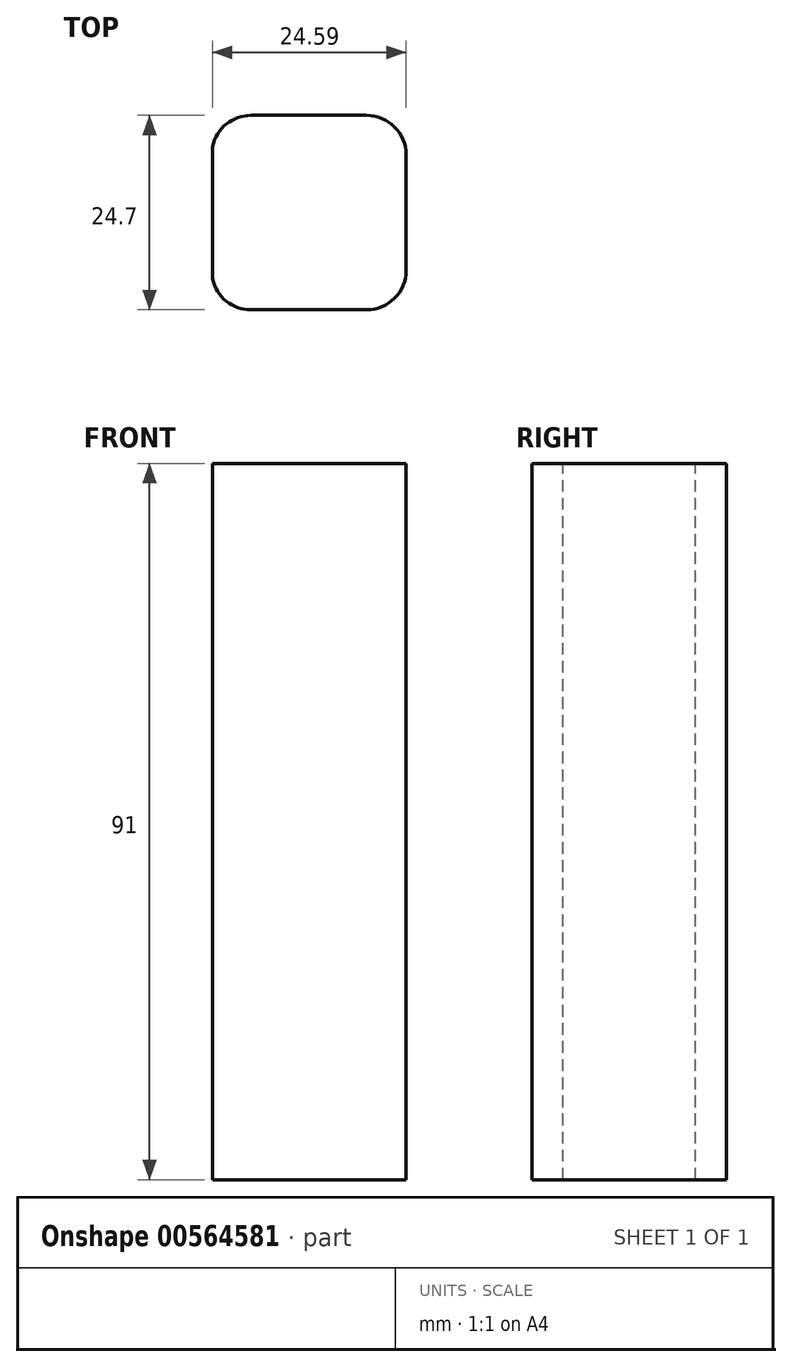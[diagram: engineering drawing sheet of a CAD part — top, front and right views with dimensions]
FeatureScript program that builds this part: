
annotation { "Feature Type Name" : "Feature", "Feature Type Description" : "" }
export const myFeature = defineFeature(function(context is Context, id is Id, definition is map)
    precondition{}
    {
        {
            var Q0;
            Q0=qCreatedBy(makeId("Top.planeOp"),FACE);
            var sketch = newSketch(context, id + "F0", { "sketchPlane" : qUnion([Q0])});
            skLineSegment(sketch, "E0.bottom", {"start": v(-40, 30) * mm, "end": v(40, 30) * mm});
            skLineSegment(sketch, "E0.top", {"start": v(-40, -30) * mm, "end": v(40, -30) * mm});
            skLineSegment(sketch, "E0.left", {"start": v(-40, 30) * mm, "end": v(-40, -30) * mm});
            skLineSegment(sketch, "E0.right", {"start": v(40, 30) * mm, "end": v(40, -30) * mm});
            skPoint(sketch, "E0.middle", {"position": v(0, 0) * mm});
            skSolve(sketch);
        }
        {
            var Q0;
            Q0=makeQuery(id+"F0.imprint","IMPRINT",FACE,{"disambiguationData":[TD([[makeQuery(id+"F0.imprint","IMPRINT",EDGE,{"derivedFrom":sQuery(id+"F0.wireOp",EDGE,"E0.bottom")}),-1.0]])]});
            extrude(context, id + "F1", {"entities" : qUnion([Q0]), "depth" : 130 * mm});
        }
        {
            var Q0;
            Q0=makeQuery(id+"F1.opExtrude","CAP_FACE",FACE,{"disambiguationData":[OSD([sQuery(id+"F0.wireOp",EDGE,"E0.bottom"),sQuery(id+"F0.wireOp",EDGE,"E0.top"),sQuery(id+"F0.wireOp",EDGE,"E0.left"),sQuery(id+"F0.wireOp",EDGE,"E0.right")])],"isStart":false});
            shell(context, id + "F2", {"entities" : qUnion([Q0]), "thickness" : 1.5 * mm});
        }
        {
            var Q0;
            Q0=makeQuery(id+"F2.opShell","OFFSET_FACE",FACE,{"disambiguationData":[OSD([sQuery(id+"F0.wireOp",EDGE,"E0.bottom"),sQuery(id+"F0.wireOp",EDGE,"E0.top"),sQuery(id+"F0.wireOp",EDGE,"E0.left"),sQuery(id+"F0.wireOp",EDGE,"E0.right")])]});
            var sketch = newSketch(context, id + "F3", { "sketchPlane" : qUnion([Q0])});
            skLineSegment(sketch, "E1.bottom", {"start": v(11, -28.5) * mm, "end": v(12.5, -28.5) * mm});
            skLineSegment(sketch, "E1.top", {"start": v(11, -1.5) * mm, "end": v(12.5, -1.5) * mm});
            skLineSegment(sketch, "E1.left", {"start": v(11, -28.5) * mm, "end": v(11, -1.5) * mm});
            skLineSegment(sketch, "E1.right", {"start": v(12.5, -28.5) * mm, "end": v(12.5, -1.5) * mm});
            skSolve(sketch);
        }
        {
            var Q0;
            Q0=qSketchRegion(id+"F3",true);
            extrude(context, id + "F4", {"entities" : qUnion([Q0]), "operationType" : NewBodyOperationType.ADD, "depth" : 91 * mm});
        }
        {
            var Q0;
            {var subQ0=sQuery(id+"F0.wireOp",EDGE,"E0.bottom");Q0=makeQuery(id+"F2.opShell","OFFSET_EDGE",EDGE,{"disambiguationData":[OSD([subQ0]),TDD([makeQuery(id+"F1.opExtrude","CAP_EDGE",EDGE,{"disambiguationData":[OSD([subQ0])],"isStart":true})])]});}
            var Q1;
            {var subQ0=sQuery(id+"F0.wireOp",EDGE,"E0.left");Q1=makeQuery(id+"F2.opShell","OFFSET_EDGE",EDGE,{"disambiguationData":[OSD([subQ0]),TDD([makeQuery(id+"F1.opExtrude","CAP_EDGE",EDGE,{"disambiguationData":[OSD([subQ0])],"isStart":true})])]});}
            var Q2;
            {var subQ0=sQuery(id+"F0.wireOp",EDGE,"E0.left");var subQ1=sQuery(id+"F0.wireOp",EDGE,"E0.top");Q2=makeQuery(id+"F4.boolean.opBoolean","SPLIT",EDGE,{"disambiguationData":[TD([makeQuery(id+"F2.opShell","OFFSET_FACE",FACE,{"disambiguationData":[OSD([subQ0])]})])],"derivedFrom":makeQuery(id+"F2.opShell","OFFSET_EDGE",EDGE,{"disambiguationData":[OSD([subQ1]),TDD([makeQuery(id+"F1.opExtrude","CAP_EDGE",EDGE,{"disambiguationData":[OSD([subQ1])],"isStart":true})])]})});}
            var Q3;
            Q3=makeQuery(id+"F4.opExtrude","CAP_EDGE",EDGE,{"disambiguationData":[OSD([sQuery(id+"F3.wireOp",EDGE,"E1.left")])],"isStart":true});
            fillet(context, id + "F5", {"entities" : qUnion([Q0, Q1, Q2, Q3]), "radius" : 1 * mm, "tangentPropagation" : true, "allowEdgeOverflow" : false});
        }
        {
            var Q0;
            Q0=makeQuery(id+"F4.opExtrude","CAP_FACE",FACE,{"disambiguationData":[OSD([sQuery(id+"F3.wireOp",EDGE,"E1.bottom"),sQuery(id+"F3.wireOp",EDGE,"E1.top"),sQuery(id+"F3.wireOp",EDGE,"E1.left"),sQuery(id+"F3.wireOp",EDGE,"E1.right")])],"isStart":false});
            var sketch = newSketch(context, id + "F6", { "sketchPlane" : qUnion([Q0])});
            skLineSegment(sketch, "E2.bottom", {"start": v(11, -1.5) * mm, "end": v(38.47, -1.5) * mm});
            skLineSegment(sketch, "E2.top", {"start": v(11, -28.53) * mm, "end": v(38.47, -28.53) * mm});
            skLineSegment(sketch, "E2.left", {"start": v(11, -1.5) * mm, "end": v(11, -28.53) * mm});
            skLineSegment(sketch, "E2.right", {"start": v(38.47, -1.5) * mm, "end": v(38.47, -28.53) * mm});
            skLineSegment(sketch, "E3.bottom", {"start": v(33.24, -7) * mm, "end": v(16.24, -7) * mm});
            skLineSegment(sketch, "E3.top", {"start": v(33.24, -23) * mm, "end": v(16.24, -23) * mm});
            skLineSegment(sketch, "E3.left", {"start": v(33.24, -7) * mm, "end": v(33.24, -23) * mm});
            skLineSegment(sketch, "E3.right", {"start": v(16.24, -7) * mm, "end": v(16.24, -23) * mm});
            skPoint(sketch, "E3.middle", {"position": v(24.74, -15) * mm});
            skPoint(sketch, "E3.middle.positionSnap0", {"position": v(12.5, -15) * mm});
            skPoint(sketch, "E3.middle.positionSnap1", {"position": v(24.74, -1.5) * mm});
            skPoint(sketch, "E3.centerSnap0", {"position": v(12.5, -15) * mm});
            skPoint(sketch, "E3.centerSnap1", {"position": v(24.74, -1.5) * mm});
            skSolve(sketch);
        }
        {
            var Q0;
            {var subQ0=sQuery(id+"F6.wireOp",EDGE,"E2.top");Q0=makeQuery(id+"F6.imprint","IMPRINT",FACE,{"disambiguationData":[TD([[makeQuery(id+"F6.imprint","IMPRINT",EDGE,{"derivedFrom":subQ0}),1.0]])]});}
            var Q1;
            {var subQ3=makeQuery(id+"F4.opExtrude","CAP_EDGE",EDGE,{"disambiguationData":[OSD([sQuery(id+"F3.wireOp",EDGE,"E1.right")])],"isStart":false});Q1=makeQuery(id+"F6.imprint","IMPRINT",FACE,{"disambiguationData":[TD([[makeQuery(id+"F6.imprint","IMPRINT",EDGE,{"derivedFrom":subQ3}),1.0]])]});}
            extrude(context, id + "F7", {"entities" : qUnion([Q0, Q1]), "operationType" : NewBodyOperationType.ADD, "depth" : 2 * mm});
        }
        {
            var Q0;
            Q0=makeQuery(id+"F7.boolean.opBoolean","INTERSECT",EDGE,{"derivedFrom":[makeQuery(id+"F2.opShell","OFFSET_FACE",FACE,{"disambiguationData":[OSD([sQuery(id+"F0.wireOp",EDGE,"E0.top")])]}),makeQuery(id+"F7.opExtrude","SWEPT_FACE",FACE,{"disambiguationData":[OSD([sQuery(id+"F6.wireOp",EDGE,"E2.left")])]})]});
            var Q1;
            Q1=makeQuery(id+"F7.boolean.opBoolean","INTERSECT",EDGE,{"derivedFrom":[makeQuery(id+"F2.opShell","OFFSET_FACE",FACE,{"disambiguationData":[OSD([sQuery(id+"F0.wireOp",EDGE,"E0.top")])]}),makeQuery(id+"F7.opExtrude","CAP_FACE",FACE,{"disambiguationData":[OSD([sQuery(id+"F6.wireOp",EDGE,"E2.bottom"),sQuery(id+"F6.wireOp",EDGE,"E2.top"),sQuery(id+"F6.wireOp",EDGE,"E2.left"),sQuery(id+"F6.wireOp",EDGE,"E2.right"),sQuery(id+"F6.wireOp",EDGE,"E3.bottom"),sQuery(id+"F6.wireOp",EDGE,"E3.top"),sQuery(id+"F6.wireOp",EDGE,"E3.left"),sQuery(id+"F6.wireOp",EDGE,"E3.right")])],"isStart":false})]});
            fillet(context, id + "F8", {"entities" : qUnion([Q0, Q1]), "radius" : 1 * mm, "tangentPropagation" : true, "allowEdgeOverflow" : false});
        }
        {
            var Q0;
            {var subQ0=sQuery(id+"F0.wireOp",EDGE,"E0.left");var subQ1=sQuery(id+"F0.wireOp",EDGE,"E0.top");Q0=makeQuery(id+"FWzvhFEn40ZoO8K_2.boolean.opBoolean","SPLIT",EDGE,{"disambiguationData":[TD([makeQuery(id+"F5.opFillet","BLEND_FACE",FACE,{"disambiguationData":[OSD([subQ0])]})])],"derivedFrom":makeQuery(id+"F2.opShell","OFFSET_EDGE",EDGE,{"disambiguationData":[OSD([subQ1,subQ0])]})});}
            var Q1;
            {var subQ0=sQuery(id+"F0.wireOp",EDGE,"E0.left");var subQ1=sQuery(id+"F0.wireOp",EDGE,"E0.bottom");Q1=makeQuery(id+"FWzvhFEn40ZoO8K_2.boolean.opBoolean","SPLIT",EDGE,{"disambiguationData":[TD([makeQuery(id+"F5.opFillet","BLEND_FACE",FACE,{"disambiguationData":[OSD([subQ1])]})])],"derivedFrom":makeQuery(id+"F2.opShell","OFFSET_EDGE",EDGE,{"disambiguationData":[OSD([subQ1,subQ0])]})});}
            var Q2;
            {var subQ0=sQuery(id+"F0.wireOp",EDGE,"E0.bottom");var subQ1=sQuery(id+"F0.wireOp",EDGE,"E0.right");Q2=makeQuery(id+"FWzvhFEn40ZoO8K_2.boolean.opBoolean","SPLIT",EDGE,{"disambiguationData":[TD([makeQuery(id+"F5.opFillet","BLEND_FACE",FACE,{"disambiguationData":[OSD([subQ0])]})])],"derivedFrom":makeQuery(id+"F2.opShell","OFFSET_EDGE",EDGE,{"disambiguationData":[OSD([subQ0,subQ1])]})});}
            fillet(context, id + "F9", {"entities" : qUnion([Q0, Q1, Q2]), "radius" : 1 * mm, "tangentPropagation" : true, "allowEdgeOverflow" : false});
        }
        {
            var Q0;
            Q0=makeQuery(id+"F1.opExtrude","SWEPT_FACE",FACE,{"disambiguationData":[OSD([sQuery(id+"F0.wireOp",EDGE,"E0.bottom")])]});
            var sketch = newSketch(context, id + "F10", { "sketchPlane" : qUnion([Q0])});
            skLineSegment(sketch, "E4.0", {"start": v(-41.4, 2.4) * mm, "end": v(-65.42, 34.39) * mm});
            skLineSegment(sketch, "E5", {"start": v(-41.4, 2.4) * mm, "end": v(-42.6, 1.5) * mm});
            skLineSegment(sketch, "E6", {"start": v(-65.42, 34.39) * mm, "end": v(-66.62, 33.49) * mm});
            skLineSegment(sketch, "E7", {"start": v(-42.6, 1.5) * mm, "end": v(-66.62, 33.49) * mm});
            skLineSegment(sketch, "E8.bottom", {"start": v(-40, 0) * mm, "end": v(-45, 0) * mm});
            skLineSegment(sketch, "E8.top", {"start": v(-40, 4) * mm, "end": v(-45, 4) * mm});
            skLineSegment(sketch, "E8.left", {"start": v(-40, 0) * mm, "end": v(-40, 4) * mm});
            skLineSegment(sketch, "E8.right", {"start": v(-45, 0) * mm, "end": v(-45, 4) * mm});
            skLineSegment(sketch, "E9.bottom", {"start": v(-40, 32.63) * mm, "end": v(-68, 32.63) * mm});
            skLineSegment(sketch, "E9.top", {"start": v(-40, 35.63) * mm, "end": v(-68, 35.63) * mm});
            skLineSegment(sketch, "E9.left", {"start": v(-40, 32.63) * mm, "end": v(-40, 35.63) * mm});
            skLineSegment(sketch, "E9.right", {"start": v(-68, 32.63) * mm, "end": v(-68, 35.63) * mm});
            skSolve(sketch);
        }
        {
            var Q0;
            {var subQ1=sQuery(id+"F10.wireOp",EDGE,"E5");Q0=makeQuery(id+"F10.imprint","IMPRINT",FACE,{"disambiguationData":[TD([[makeQuery(id+"F10.imprint","IMPRINT",EDGE,{"derivedFrom":subQ1}),1.0]])]});}
            extrude(context, id + "F11", {"entities" : qUnion([Q0]), "operationType" : NewBodyOperationType.ADD, "oppositeDirection" : true, "depth" : 60 * mm});
        }
        {
            var Q0;
            {var subQ1=sQuery(id+"F10.wireOp",EDGE,"E6");Q0=makeQuery(id+"F10.imprint","IMPRINT",FACE,{"disambiguationData":[TD([[makeQuery(id+"F10.imprint","IMPRINT",EDGE,{"derivedFrom":subQ1}),-1.0]])]});}
            extrude(context, id + "F12", {"entities" : qUnion([Q0]), "operationType" : NewBodyOperationType.ADD, "oppositeDirection" : true, "depth" : 60 * mm});
        }
        {
            var Q0;
            {var subQ0=sQuery(id+"F10.wireOp",EDGE,"E5");Q0=makeQuery(id+"F10.imprint","IMPRINT",FACE,{"disambiguationData":[TD([[makeQuery(id+"F10.imprint","IMPRINT",EDGE,{"derivedFrom":subQ0}),-1.0]])]});}
            var Q1;
            {var subQ0=sQuery(id+"F10.wireOp",EDGE,"E8.top");var subQ1=sQuery(id+"F10.wireOp",EDGE,"E4.0");var subQ2=makeQuery(id+"F10.imprint","INTERSECT",VERTEX,{"derivedFrom":[subQ1,subQ0]});Q1=makeQuery(id+"F10.imprint","IMPRINT",FACE,{"disambiguationData":[TD([[makeQuery(id+"F10.imprint","IMPRINT",EDGE,{"disambiguationData":[TD([[subQ2,-1.0]])],"derivedFrom":subQ1}),1.0]])]});}
            var Q2;
            {var subQ0=sQuery(id+"F10.wireOp",EDGE,"E6");Q2=makeQuery(id+"F10.imprint","IMPRINT",FACE,{"disambiguationData":[TD([[makeQuery(id+"F10.imprint","IMPRINT",EDGE,{"derivedFrom":subQ0}),1.0]])]});}
            var Q3;
            Q3=sQuery(id+"F10.wireOp",EDGE,"E7");
            var Q4;
            Q4=sQuery(id+"F10.wireOp",EDGE,"E4.0");
            var Q5;
            Q5=sQuery(id+"F10.wireOp",EDGE,"E6");
            var Q6;
            Q6=sQuery(id+"F10.wireOp",EDGE,"E5");
            extrude(context, id + "F13", {"entities" : qUnion([Q0, Q1, Q2]), "surfaceEntities" : qUnion([Q3, Q4, Q5, Q6]), "oppositeDirection" : true, "depth" : 50 * mm});
        }
        {
            var Q0;
            Q0=makeQuery(id+"F12.opExtrude","SWEPT_EDGE",EDGE,{"disambiguationData":[OSD([sQuery(id+"F0.wireOp",EDGE,"E0.bottom"),sQuery(id+"F0.wireOp",EDGE,"E0.right"),sQuery(id+"F10.wireOp",EDGE,"E9.top"),sQuery(id+"F10.wireOp",EDGE,"E9.left")])]});
            var Q1;
            Q1=makeQuery(id+"F11.opExtrude","SWEPT_EDGE",EDGE,{"disambiguationData":[OSD([sQuery(id+"F0.wireOp",EDGE,"E0.bottom"),sQuery(id+"F0.wireOp",EDGE,"E0.right"),sQuery(id+"F10.wireOp",EDGE,"E8.top"),sQuery(id+"F10.wireOp",EDGE,"E8.left")])]});
            var Q2;
            Q2=makeQuery(id+"F12.opExtrude","SWEPT_EDGE",EDGE,{"disambiguationData":[OSD([sQuery(id+"F0.wireOp",EDGE,"E0.bottom"),sQuery(id+"F0.wireOp",EDGE,"E0.right"),sQuery(id+"F10.wireOp",EDGE,"E9.bottom"),sQuery(id+"F10.wireOp",EDGE,"E9.left")])]});
            fillet(context, id + "F14", {"entities" : qUnion([Q0, Q1, Q2]), "radius" : 2 * mm, "tangentPropagation" : true, "allowEdgeOverflow" : false});
        }
        {
            var Q0;
            Q0=makeQuery(id+"F7.opExtrude","CAP_FACE",FACE,{"disambiguationData":[OSD([sQuery(id+"F6.wireOp",EDGE,"E2.bottom"),sQuery(id+"F6.wireOp",EDGE,"E2.top"),sQuery(id+"F6.wireOp",EDGE,"E2.left"),sQuery(id+"F6.wireOp",EDGE,"E2.right"),sQuery(id+"F6.wireOp",EDGE,"E3.bottom"),sQuery(id+"F6.wireOp",EDGE,"E3.top"),sQuery(id+"F6.wireOp",EDGE,"E3.left"),sQuery(id+"F6.wireOp",EDGE,"E3.right")])],"isStart":true});
            var sketch = newSketch(context, id + "F15", { "sketchPlane" : qUnion([Q0])});
            skLineSegment(sketch, "E10.bottom", {"start": v(17.39, 2.65) * mm, "end": v(32.09, 2.65) * mm});
            skLineSegment(sketch, "E10.top", {"start": v(17.39, 27.35) * mm, "end": v(32.09, 27.35) * mm});
            skLineSegment(sketch, "E10.left", {"start": v(12.39, 7.65) * mm, "end": v(12.39, 22.35) * mm});
            skLineSegment(sketch, "E10.right", {"start": v(37.09, 7.65) * mm, "end": v(37.09, 22.35) * mm});
            skPoint(sketch, "E10.middle", {"position": v(24.74, 15) * mm});
            skPoint(sketch, "E10.middle.positionSnap0", {"position": v(24.74, 23) * mm});
            skPoint(sketch, "E10.middle.positionSnap1", {"position": v(33.24, 15) * mm});
            skPoint(sketch, "E10.centerSnap0", {"position": v(24.74, 23) * mm});
            skPoint(sketch, "E10.centerSnap1", {"position": v(33.24, 15) * mm});
            skPoint(sketch, "E11.visualSharp", {"position": v(12.39, 2.65) * mm});
            skArc(sketch, "E11.filletArc", {"start": v(12.39, 7.65) * mm, "mid": v(13.85, 4.11) * mm, "end": v(17.39, 2.65) * mm});
            skPoint(sketch, "E12.visualSharp", {"position": v(12.39, 27.35) * mm});
            skArc(sketch, "E12.filletArc", {"start": v(17.39, 27.35) * mm, "mid": v(13.85, 25.89) * mm, "end": v(12.39, 22.35) * mm});
            skPoint(sketch, "E13.visualSharp", {"position": v(37.09, 27.35) * mm});
            skArc(sketch, "E13.filletArc", {"start": v(37.09, 22.35) * mm, "mid": v(35.62, 25.89) * mm, "end": v(32.09, 27.35) * mm});
            skPoint(sketch, "E14.visualSharp", {"position": v(37.09, 2.65) * mm});
            skArc(sketch, "E14.filletArc", {"start": v(32.09, 2.65) * mm, "mid": v(35.62, 4.11) * mm, "end": v(37.09, 7.65) * mm});
            skSolve(sketch);
        }
        {
            var Q0;
            {var subQ1=sQuery(id+"F15.wireOp",EDGE,"E10.bottom");Q0=makeQuery(id+"F15.imprint","IMPRINT",FACE,{"disambiguationData":[TD([[makeQuery(id+"F15.imprint","IMPRINT",EDGE,{"derivedFrom":subQ1}),1.0]])]});}
            var Q1;
            Q1=makeQuery(id+"F15.imprint","IMPRINT",FACE,{"disambiguationData":[TD([[makeQuery(id+"F15.imprint","IMPRINT",EDGE,{"derivedFrom":makeQuery(id+"F7.opExtrude","CAP_EDGE",EDGE,{"disambiguationData":[OSD([sQuery(id+"F6.wireOp",EDGE,"E3.bottom")])],"isStart":true})}),-1.0]])]});
            extrude(context, id + "F16", {"entities" : qUnion([Q0, Q1]), "depth" : 91 * mm});
        }
        {
            var Q0;
            Q0=makeQuery(id+"F1.opExtrude","SWEPT_BODY",BODY,{"disambiguationData":[OSD([sQuery(id+"F0.wireOp",EDGE,"E0.bottom"),sQuery(id+"F0.wireOp",EDGE,"E0.top"),sQuery(id+"F0.wireOp",EDGE,"E0.left"),sQuery(id+"F0.wireOp",EDGE,"E0.right")])]});
            deleteBodies(context, id + "F17", {"entities" : qUnion([Q0])});
        }
        {
            var Q0;
            Q0=makeQuery(id+"F13.opExtrude","SWEPT_BODY",BODY,{"disambiguationData":[OSD([sQuery(id+"F10.wireOp",EDGE,"E4.0"),sQuery(id+"F10.wireOp",EDGE,"E5"),sQuery(id+"F10.wireOp",EDGE,"E6"),sQuery(id+"F10.wireOp",EDGE,"E7")])]});
            deleteBodies(context, id + "F18", {"entities" : qUnion([Q0])});
        }
    });
